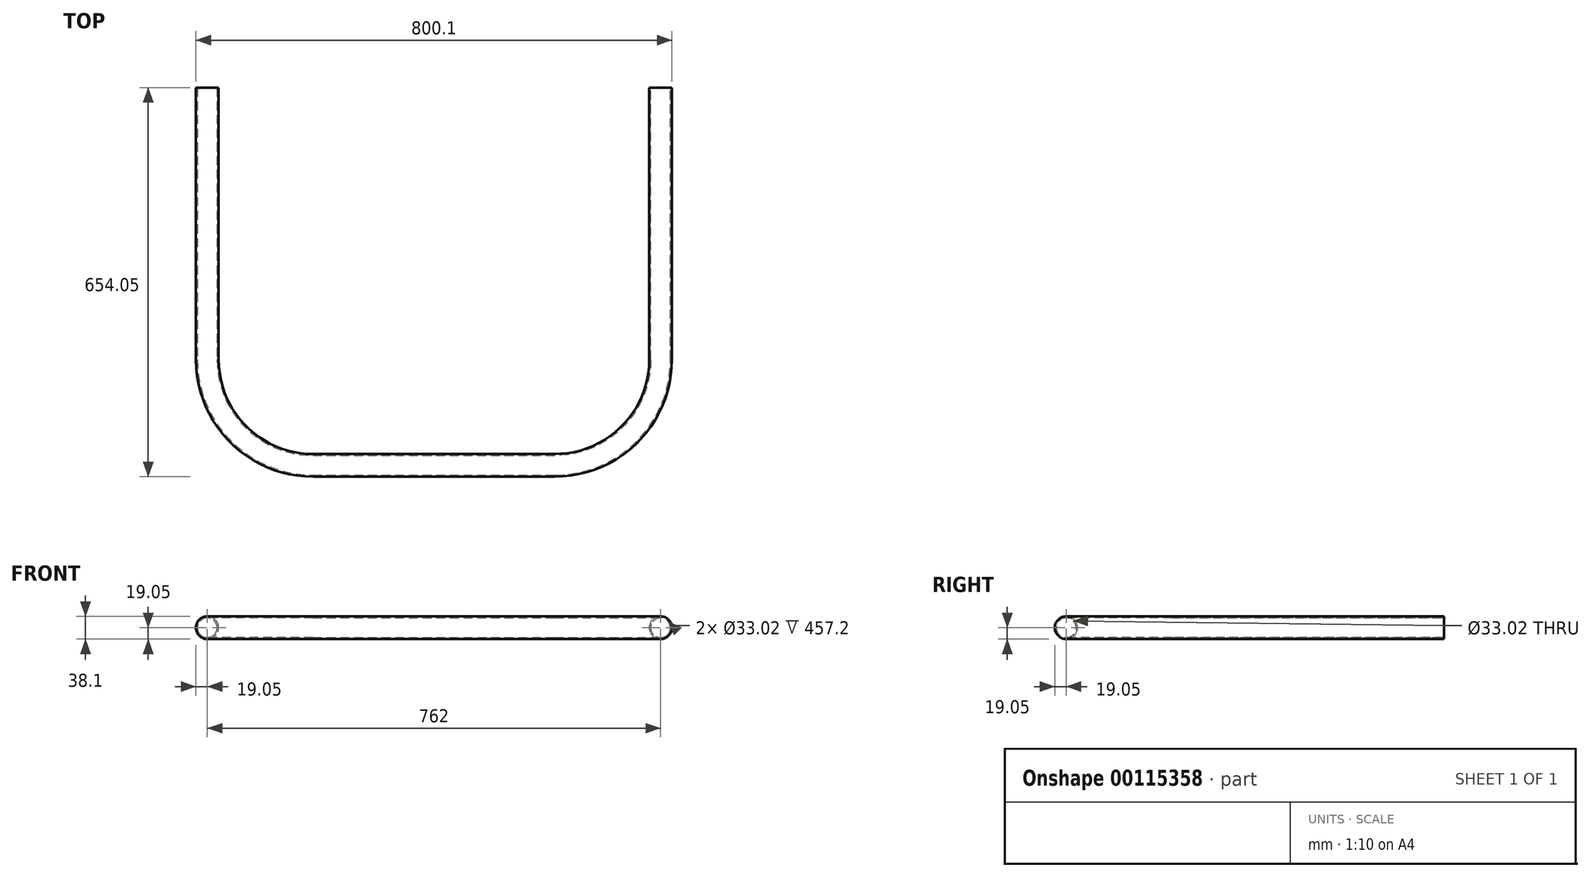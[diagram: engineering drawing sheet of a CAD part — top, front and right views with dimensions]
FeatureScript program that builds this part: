
annotation { "Feature Type Name" : "Feature", "Feature Type Description" : "" }
export const myFeature = defineFeature(function(context is Context, id is Id, definition is map)
    precondition{}
    {
        {
            var Q0;
            Q0=qCreatedBy(makeId("Top.planeOp"),FACE);
            var sketch = newSketch(context, id + "F0", { "sketchPlane" : qUnion([Q0])});
            skLineSegment(sketch, "E0", {"start": v(-381, 635) * mm, "end": v(-381, 177.8) * mm});
            skLineSegment(sketch, "E1", {"start": v(-203.2, 0) * mm, "end": v(203.2, 0) * mm});
            skLineSegment(sketch, "E2", {"start": v(381, 177.8) * mm, "end": v(381, 635) * mm});
            skLineSegment(sketch, "E3", {"start": v(-398.81, 635) * mm, "end": v(413.4, 635) * mm, "construction": true});
            skLineSegment(sketch, "E4", {"start": v(0, 73.8) * mm, "end": v(0, -49.52) * mm, "construction": true});
            skPoint(sketch, "E5.visualSharp", {"position": v(-381, 0) * mm});
            skArc(sketch, "E5.filletArc", {"start": v(-381, 177.8) * mm, "mid": v(-328.92, 52.08) * mm, "end": v(-203.2, 0) * mm});
            skPoint(sketch, "E6.visualSharp", {"position": v(381, 0) * mm});
            skArc(sketch, "E6.filletArc", {"start": v(203.2, 0) * mm, "mid": v(328.92, 52.08) * mm, "end": v(381, 177.8) * mm});
            skSolve(sketch);
        }
        {
            var Q0;
            Q0=sQuery(id+"F0.wireOp",VERTEX,"E0.start");
            var Q1;
            Q1=sQuery(id+"F0.wireOp",EDGE,"E0");
            cPlane(context, id + "F1", {"entities" : qUnion([Q0, Q1]), "cplaneType" : CPlaneType.LINE_POINT, "offset" : 0 * mm, "width" : 152.4 * mm, "height" : 152.4 * mm});
        }
        {
            var Q0;
            Q0=qCreatedBy(id+"F1.planeOp",FACE);
            var sketch = newSketch(context, id + "F2", { "sketchPlane" : qUnion([Q0])});
            skCircle(sketch, "E7", {"center": v(-381, 0) * mm, "radius": 19.05 * mm});
            skSolve(sketch);
        }
        {
            var Q0;
            Q0=makeQuery(id+"F2.imprint","IMPRINT",FACE,{"disambiguationData":[TD([[makeQuery(id+"F2.imprint","IMPRINT",EDGE,{"derivedFrom":sQuery(id+"F2.wireOp",EDGE,"E7")}),1.0]])]});
            var Q1;
            Q1=sQuery(id+"F2.wireOp",EDGE,"E7");
            var Q2;
            Q2=sQuery(id+"F0.wireOp",EDGE,"E0");
            var Q3;
            Q3=sQuery(id+"F0.wireOp",EDGE,"E5.filletArc");
            var Q4;
            Q4=sQuery(id+"F0.wireOp",EDGE,"E1");
            var Q5;
            Q5=sQuery(id+"F0.wireOp",EDGE,"E6.filletArc");
            var Q6;
            Q6=sQuery(id+"F0.wireOp",EDGE,"E2");
            sweep(context, id + "F3", {"profiles" : qUnion([Q0]), "surfaceProfiles" : qUnion([Q1]), "path" : qUnion([Q2, Q3, Q4, Q5, Q6])});
        }
        {
            var Q0;
            Q0=makeQuery(id+"F3.opSweep","CAP_FACE",FACE,{"disambiguationData":[OSD([sQuery(id+"F0.wireOp",VERTEX,"E2.end"),sQuery(id+"F2.wireOp",EDGE,"E7")])],"isStart":false});
            var Q1;
            Q1=makeQuery(id+"F3.opSweep","CAP_FACE",FACE,{"disambiguationData":[OSD([sQuery(id+"F0.wireOp",VERTEX,"E0.start"),sQuery(id+"F2.wireOp",EDGE,"E7")])],"isStart":true});
            shell(context, id + "F4", {"entities" : qUnion([Q0, Q1]), "thickness" : 2.54 * mm});
        }
    });
